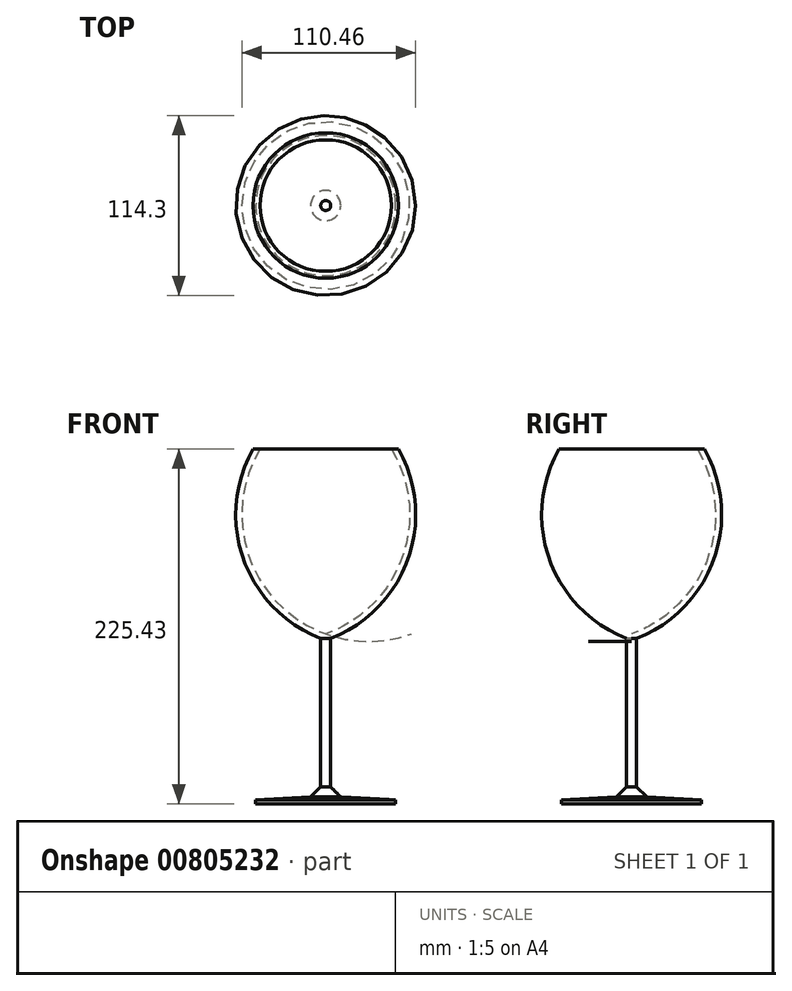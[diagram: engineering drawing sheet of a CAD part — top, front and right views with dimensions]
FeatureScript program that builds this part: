
annotation { "Feature Type Name" : "Feature", "Feature Type Description" : "" }
export const myFeature = defineFeature(function(context is Context, id is Id, definition is map)
    precondition{}
    {
        {
            var Q0;
            Q0=qCreatedBy(makeId("Front.planeOp"),FACE);
            var sketch = newSketch(context, id + "F0", { "sketchPlane" : qUnion([Q0])});
            skLineSegment(sketch, "E0", {"start": v(0, 0) * mm, "end": v(0, -107.95) * mm});
            skLineSegment(sketch, "E1", {"start": v(0, -107.95) * mm, "end": v(44.45, -107.95) * mm});
            skLineSegment(sketch, "E2", {"start": v(44.45, -107.95) * mm, "end": v(44.45, -105.4) * mm});
            skLineSegment(sketch, "E3", {"start": v(44.45, -105.4) * mm, "end": v(9.57, -103.58) * mm});
            skLineSegment(sketch, "E4", {"start": v(9.57, -103.58) * mm, "end": v(3.17, -97.18) * mm});
            skLineSegment(sketch, "E5", {"start": v(3.18, -97.18) * mm, "end": v(3.18, -2.9) * mm});
            skArc(sketch, "E6", {"start": v(3.18, -2.9) * mm, "mid": v(52.23, 47.44) * mm, "end": v(46.18, 117.48) * mm});
            skArc(sketch, "E7", {"start": v(0, 0) * mm, "mid": v(48.66, 48.86) * mm, "end": v(41.74, 117.48) * mm});
            skLineSegment(sketch, "E8", {"start": v(41.74, 117.48) * mm, "end": v(46.18, 117.48) * mm});
            skSolve(sketch);
        }
        {
            var Q0;
            Q0=qSketchRegion(id+"F0",true);
            var Q1;
            Q1=sQuery(id+"F0.wireOp",EDGE,"E0");
            revolve(context, id + "F1", {"entities" : qUnion([Q0]), "axis" : qUnion([Q1]), "revolveType" : RevolveType.FULL});
        }
    });
